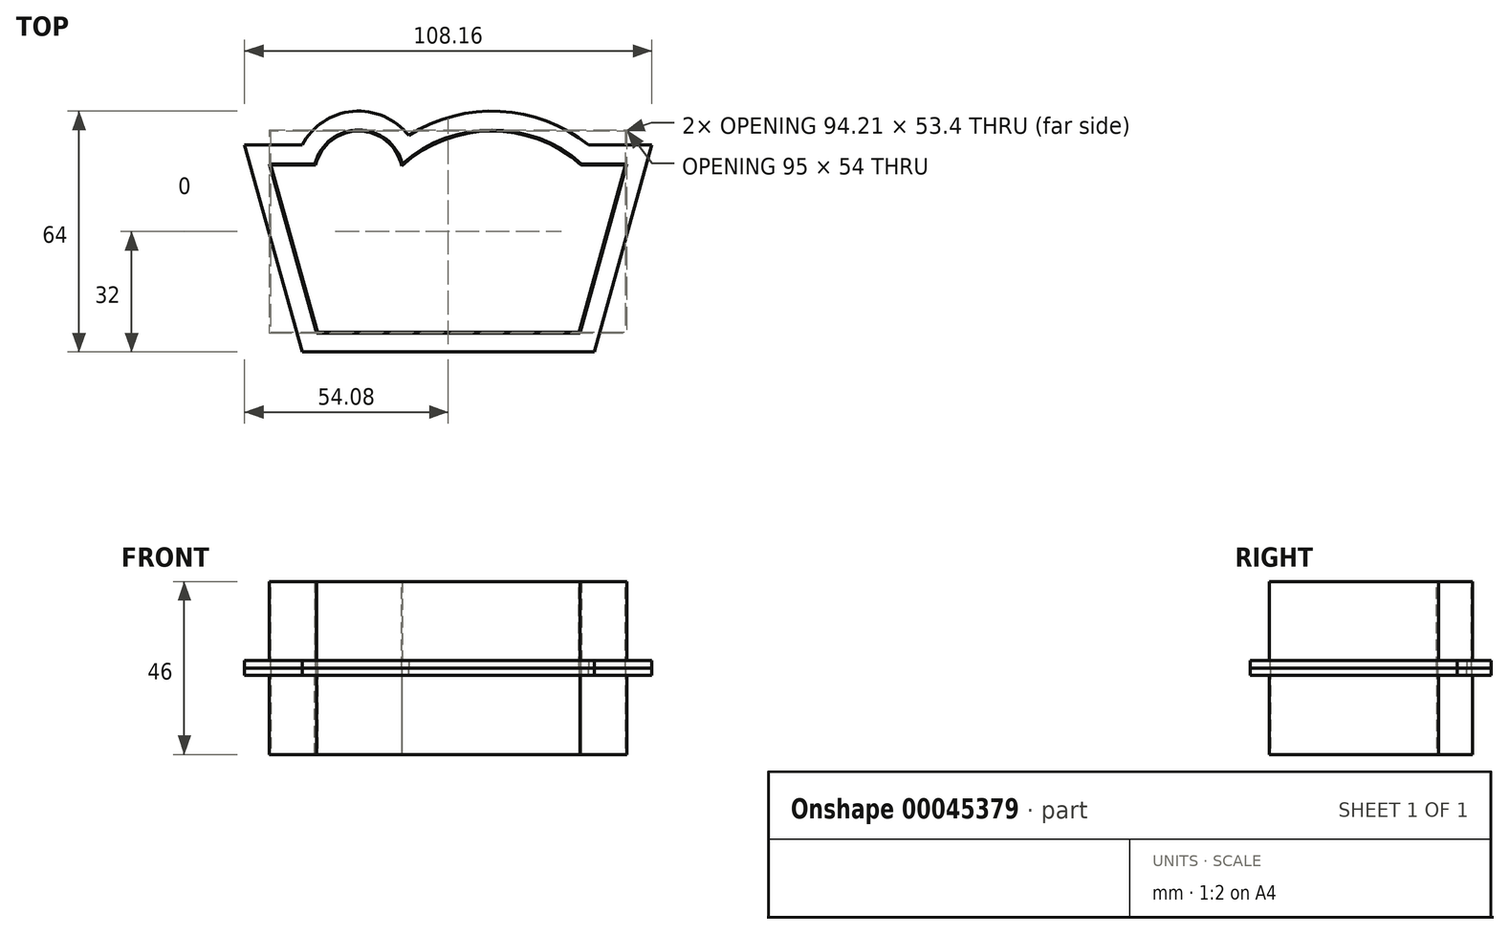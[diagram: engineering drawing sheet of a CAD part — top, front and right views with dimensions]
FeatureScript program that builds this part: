
annotation { "Feature Type Name" : "Feature", "Feature Type Description" : "" }
export const myFeature = defineFeature(function(context is Context, id is Id, definition is map)
    precondition{}
    {
        {
            var Q0;
            Q0=qCreatedBy(makeId("Top.planeOp"),FACE);
            var sketch = newSketch(context, id + "F0", { "sketchPlane" : qUnion([Q0])});
            skLineSegment(sketch, "E0", {"start": v(-47.5, 45) * mm, "end": v(-35, 0) * mm});
            skLineSegment(sketch, "E1", {"start": v(-35, 0) * mm, "end": v(35, 0) * mm});
            skLineSegment(sketch, "E2", {"start": v(35, 0) * mm, "end": v(47.5, 45) * mm});
            skLineSegment(sketch, "E3", {"start": v(47.5, 45) * mm, "end": v(35.43, 45) * mm});
            skArc(sketch, "E4", {"start": v(-12.2, 45) * mm, "mid": v(-23.81, 54) * mm, "end": v(-35.43, 45) * mm});
            skArc(sketch, "E5", {"start": v(35.43, 45) * mm, "mid": v(11.62, 54) * mm, "end": v(-12.2, 45) * mm});
            skLineSegment(sketch, "E6.trimOffspring", {"start": v(-35.43, 45) * mm, "end": v(-47.5, 45) * mm});
            skLineSegment(sketch, "E7", {"start": v(-23.81, 54) * mm, "end": v(11.62, 54) * mm, "construction": true});
            skSolve(sketch);
        }
        {
            var Q0;
            Q0=qCreatedBy(makeId("Top.planeOp"),FACE);
            var sketch = newSketch(context, id + "F1", { "sketchPlane" : qUnion([Q0])});
            skArc(sketch, "E8.0", {"start": v(-10.47, 52.54) * mm, "mid": v(-25.33, 58.93) * mm, "end": v(-38.81, 50) * mm});
            skArc(sketch, "E8.1", {"start": v(37.25, 50) * mm, "mid": v(13.8, 58.94) * mm, "end": v(-10.47, 52.54) * mm});
            skLineSegment(sketch, "E8.2", {"start": v(-54.08, 50) * mm, "end": v(-38.8, -5) * mm});
            skLineSegment(sketch, "E8.3", {"start": v(-38.8, -5) * mm, "end": v(38.8, -5) * mm});
            skLineSegment(sketch, "E8.4", {"start": v(38.8, -5) * mm, "end": v(54.08, 50) * mm});
            skLineSegment(sketch, "E8.5", {"start": v(-38.81, 50) * mm, "end": v(-54.08, 50) * mm});
            skLineSegment(sketch, "E8.6", {"start": v(54.08, 50) * mm, "end": v(37.25, 50) * mm});
            skSolve(sketch);
        }
        {
            var Q0;
            Q0 = qSketchRegion(id + "F1", true);
            extrude(context, id + "F2", {"entities" : qUnion([Q0]), "depth" : 2 * mm});
        }
        {
            var Q0;
            Q0 = qSketchRegion(id + "F0", true);
            extrude(context, id + "F3", {"entities" : qUnion([Q0]), "operationType" : NewBodyOperationType.ADD, "depth" : 23 * mm});
        }
        {
            var Q0;
            Q0=makeQuery(id+"F3.opExtrude","CAP_FACE",FACE,{"disambiguationData":[OSD([sQuery(id+"F0.wireOp",EDGE,"E0"),sQuery(id+"F0.wireOp",EDGE,"E1"),sQuery(id+"F0.wireOp",EDGE,"E2"),sQuery(id+"F0.wireOp",EDGE,"E3"),sQuery(id+"F0.wireOp",EDGE,"E4"),sQuery(id+"F0.wireOp",EDGE,"E5"),sQuery(id+"F0.wireOp",EDGE,"E6.trimOffspring")])],"isStart":false});
            var sketch = newSketch(context, id + "F4", { "sketchPlane" : qUnion([Q0])});
            skArc(sketch, "E9.0", {"start": v(-12.37, 44.44) * mm, "mid": v(-23.68, 53.7) * mm, "end": v(-35.2, 44.7) * mm});
            skArc(sketch, "E9.1", {"start": v(35.32, 44.7) * mm, "mid": v(11.42, 53.7) * mm, "end": v(-12.37, 44.44) * mm});
            skLineSegment(sketch, "E9.2", {"start": v(-47.1, 44.7) * mm, "end": v(-34.77, 0.3) * mm});
            skLineSegment(sketch, "E9.3", {"start": v(-34.77, 0.3) * mm, "end": v(34.77, 0.3) * mm});
            skLineSegment(sketch, "E9.4", {"start": v(34.77, 0.3) * mm, "end": v(47.1, 44.7) * mm});
            skLineSegment(sketch, "E9.5", {"start": v(-35.2, 44.7) * mm, "end": v(-47.1, 44.7) * mm});
            skLineSegment(sketch, "E9.6", {"start": v(47.1, 44.7) * mm, "end": v(35.32, 44.7) * mm});
            skSolve(sketch);
        }
        {
            var Q0;
            Q0 = qSketchRegion(id + "F4", true);
            extrude(context, id + "F5", {"entities" : qUnion([Q0]), "operationType" : NewBodyOperationType.REMOVE, "endBound" : BoundingType.UP_TO_NEXT, "oppositeDirection" : true, "depth" : 25 * mm});
        }
        {
            var Q0;
            Q0=makeQuery(id+"F2.opExtrude","SWEPT_BODY",BODY,{"disambiguationData":[OSD([sQuery(id+"F1.wireOp",EDGE,"E8.0"),sQuery(id+"F1.wireOp",EDGE,"E8.1"),sQuery(id+"F1.wireOp",EDGE,"E8.2"),sQuery(id+"F1.wireOp",EDGE,"E8.3"),sQuery(id+"F1.wireOp",EDGE,"E8.4"),sQuery(id+"F1.wireOp",EDGE,"E8.5"),sQuery(id+"F1.wireOp",EDGE,"E8.6")])]});
            var Q1;
            Q1=qCreatedBy(makeId("Top.planeOp"),FACE);
            mirror(context, id + "F6", {"entities" : qUnion([Q0]), "mirrorPlane" : qUnion([Q1])});
        }
    });
